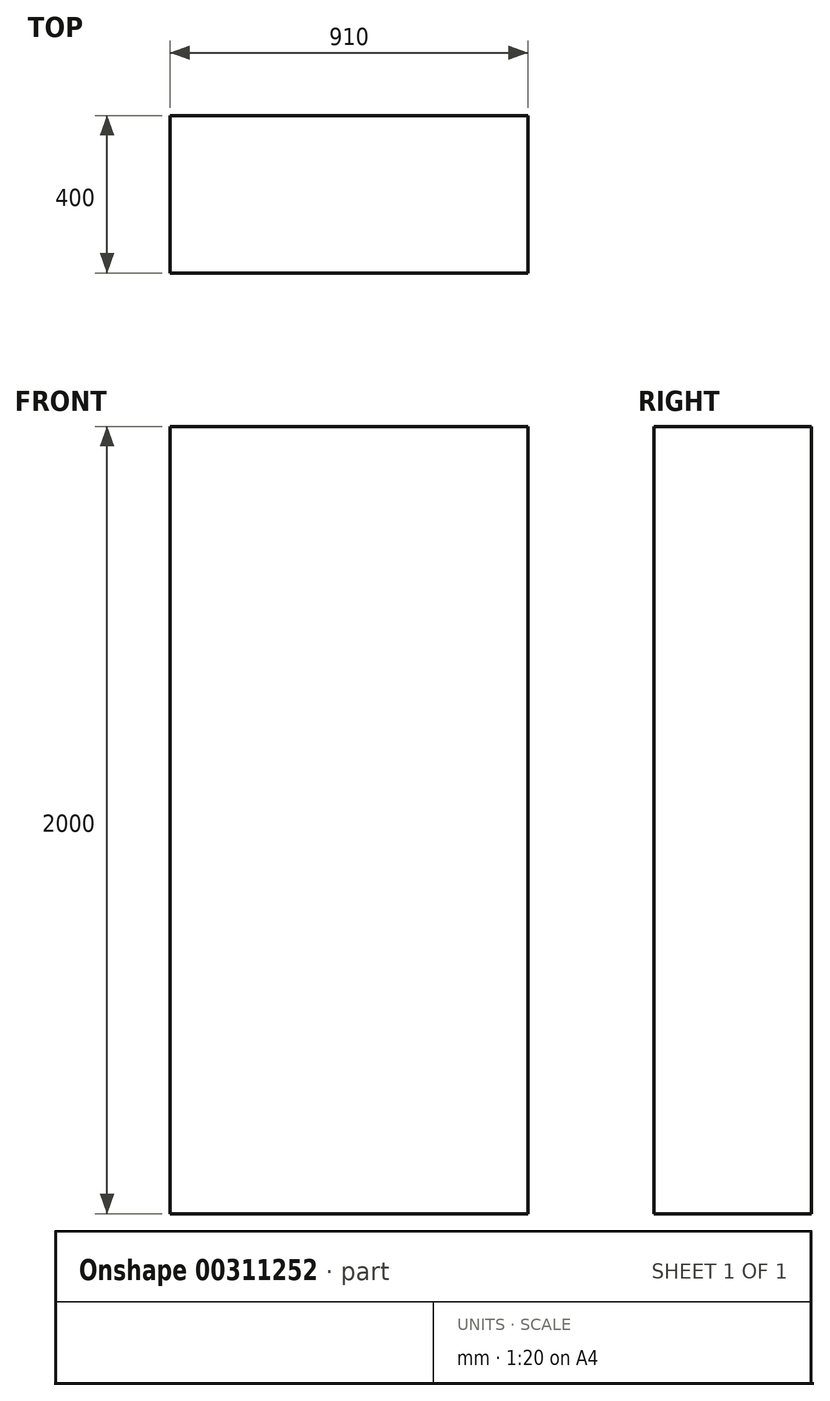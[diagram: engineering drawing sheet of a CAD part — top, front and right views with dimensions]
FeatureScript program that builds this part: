
annotation { "Feature Type Name" : "Feature", "Feature Type Description" : "" }
export const myFeature = defineFeature(function(context is Context, id is Id, definition is map)
    precondition{}
    {
        {
            var Q0;
            Q0=qCreatedBy(makeId("Front.planeOp"),FACE);
            var sketch = newSketch(context, id + "F0", { "sketchPlane" : qUnion([Q0])});
            skLineSegment(sketch, "E0.bottom", {"start": v(0, 0) * mm, "end": v(910, 0) * mm});
            skLineSegment(sketch, "E0.top", {"start": v(0, 2000) * mm, "end": v(910, 2000) * mm});
            skLineSegment(sketch, "E0.left", {"start": v(0, 0) * mm, "end": v(0, 2000) * mm});
            skLineSegment(sketch, "E0.right", {"start": v(910, 0) * mm, "end": v(910, 2000) * mm});
            skSolve(sketch);
        }
        {
            var Q0;
            Q0=makeQuery(id+"F0.imprint","IMPRINT",FACE,{"disambiguationData":[TD([[makeQuery(id+"F0.imprint","IMPRINT",EDGE,{"derivedFrom":sQuery(id+"F0.wireOp",EDGE,"E0.bottom")}),1.0]])]});
            extrude(context, id + "F1", {"entities" : qUnion([Q0]), "oppositeDirection" : true, "depth" : 400 * mm});
        }
    });
